# Revit family: ONRZ
name_source: partatom
category: Mechanical Equipment
revit_build: Autodesk Revit 2015 (Build: 20160512_1515(x64)
units: mm (PartAtom-declared; Revit-internal decimal feet)

## types (7) — shared parameters
20" Shelf = Yes
22" Shelf = Yes
Certifications = NSF 7, UL471, CSA
DATE = DOE 2017
Description = Narrow Reach-In Merchandiser
EQUIPMENT DESCRIPTION = Narrow Reach-In Merchandiser
EQUIPMENT MARK = ONRZ
GLASS = Glass
Height = 81 1/4"
Item Description = Narrow Reach-In Merchandiser
Keynote = ONRZ
Legend Number = ONRZ
Manufacturer = HILLPHOENIX
Model = ONRZ
PAINTED METAL UPPER SHELF = PAINTED SHELVES
REFRIGERATION PIPING = COPPER PIPE
STAINLESS STEEL = GALVANIZED STEEL
Size of Door = 30"
URL = http://www.hillphoenix.com
Width = 34 5/8"
left end = Yes

## per-type parameters (varying)
| type | CENTER LINE & DRAIN | DOOR CONFIGURATION | Length | Length of Cases | NUMBER OF DOORS | Type of Door Swing |
| 2 Door | 30" | MASTER DOOR : 30" X 64 3/8" 2 DOOR A SWING (LEFT OPENING) | 60" | 60" | 2 | B-Swing |
| 3 Door | 45" | MASTER DOOR : 30" X 64 3/8" 3 DOOR A SWING (LEFT OPENING) | 90" | 90" | 3 | A-Swing |
| 4 Door | 60" | MASTER DOOR : 30" X 64 3/8" 4 DOOR A SWING (LEFT OPENING) | 120" | 120" | 4 | B-Swing |
| 5 Door | 75" | MASTER DOOR : 30" X 64 3/8" 5 DOOR A SWING (LEFT OPENING) | 150" | 150" | 5 | A-Swing |
| 6 Door | 90" | MASTER DOOR : 30" X 64 3/8" 6 DOOR A SWING (LEFT OPENING) | 180" | 180" | 6 | B-Swing |
| 1 Door | 15 1/2" | MASTER DOOR : 31" X 64 3/8" 1 DOOR A SWING (LEFT OPENING) | 31" | 31" | 2 | A-Swing |
| 4 Door left pt | 60" | MASTER DOOR : 30" X 64 3/8" 4 DOOR A SWING (LEFT OPENING) | 120" | 120" | 4 | B-Swing |

## geometry (parser evidence)
native form markers: Blend x6, Sweep x25
no freeform markers — native parametric forms only
